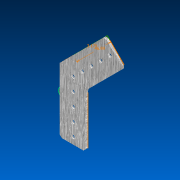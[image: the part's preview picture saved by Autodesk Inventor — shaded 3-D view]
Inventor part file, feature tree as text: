
AUTODESK INVENTOR PART (.ipt)
format: ipt  version: 2022.2 (Build 262287000, 287)  size: 128,000 bytes
history: native  units: in
note: dims shown in document units (in); Inventor stores cm internally (conversion verified against a paired STEP export)
features: other x3, sketch x1, reference x1, fillet x1
ambient origin geometry x8: Origin, YZ Plane, XZ Plane, XY Plane, X Axis, Y Axis, Z Axis, Center Point
bodies: Solid1 (feature_tree)
feature tree (6):
  sketch  "Sketch1"  dims[d1=1.85in]
  reference  "Reference1"
  fillet  "Fillet2"  Radius=0.125in
  parser-record x1  (decoder bookkeeping rows leaked as tree rows — omitted from the tree; the rows remain in map.json)
  other  "Chassis.iam"
  other  "#8-32 x 2.500 Star Drive Screw (276-8016):6"
note: 1 file-system path scrubbed to <path> (originals preserved in map.json)
